annotation { "Feature Type Name" : "Feature", "Feature Type Description" : "" }
export const myFeature = defineFeature(function(context is Context, id is Id, definition is map)
    precondition{}
    {
        {
            var Q0;
            Q0=qCreatedBy(makeId("Top.planeOp"),FACE);
            var sketch = newSketch(context, id + "F0", { "sketchPlane" : qUnion([Q0])});
            skLineSegment(sketch, "E0.bottom", {"start": v(55, -37.5) * mm, "end": v(-55, -37.5) * mm});
            skLineSegment(sketch, "E0.top", {"start": v(55, 37.5) * mm, "end": v(-55, 37.5) * mm});
            skLineSegment(sketch, "E0.left", {"start": v(55, -37.5) * mm, "end": v(55, 37.5) * mm});
            skLineSegment(sketch, "E0.right", {"start": v(-55, -37.5) * mm, "end": v(-55, 37.5) * mm});
            skPoint(sketch, "E0.middle", {"position": v(0, 0) * mm});
            skSolve(sketch);
        }
        {
            var Q0;
            Q0=makeQuery(id+"F0.imprint","IMPRINT",FACE,{"disambiguationData":[TD([[makeQuery(id+"F0.imprint","IMPRINT",EDGE,{"derivedFrom":sQuery(id+"F0.wireOp",EDGE,"E0.bottom")}),-1.0]])]});
            extrude(context, id + "F1", {"entities" : qUnion([Q0]), "depth" : 3 * mm, "offsetDistance" : 25 * mm});
        }
        {
            var Q0;
            Q0=makeQuery(id+"F1.opExtrude","CAP_FACE",FACE,{"disambiguationData":[OSD([sQuery(id+"F0.wireOp",EDGE,"E0.bottom"),sQuery(id+"F0.wireOp",EDGE,"E0.top"),sQuery(id+"F0.wireOp",EDGE,"E0.left"),sQuery(id+"F0.wireOp",EDGE,"E0.right")])],"isStart":false});
            var sketch = newSketch(context, id + "F2", { "sketchPlane" : qUnion([Q0])});
            skLineSegment(sketch, "E1.bottom", {"start": v(-55, 37.5) * mm, "end": v(-50.5, 37.5) * mm});
            skLineSegment(sketch, "E1.left", {"start": v(-55, 37.5) * mm, "end": v(-55, 32.5) * mm});
            skLineSegment(sketch, "E2.bottom", {"start": v(-55, -37.5) * mm, "end": v(-50, -37.5) * mm});
            skLineSegment(sketch, "E2.left", {"start": v(-55, -37.5) * mm, "end": v(-55, -32.5) * mm});
            skLineSegment(sketch, "E3", {"start": v(0, 31.66) * mm, "end": v(0, -14.53) * mm, "construction": true});
            skLineSegment(sketch, "E4.MirrorCS", {"start": v(-50, -37.5) * mm, "end": v(-50, -32.5) * mm});
            skLineSegment(sketch, "E5.bottom", {"start": v(55, 37.5) * mm, "end": v(50, 37.5) * mm});
            skLineSegment(sketch, "E5.left", {"start": v(55, 37.5) * mm, "end": v(55, 32.5) * mm});
            skLineSegment(sketch, "E6.bottom", {"start": v(55, -37.5) * mm, "end": v(50, -37.5) * mm});
            skLineSegment(sketch, "E6.left", {"start": v(55, -37.5) * mm, "end": v(55, -32.5) * mm});
            skCircle(sketch, "E7", {"center": v(-50.5, 33) * mm, "radius": 1.5 * mm});
            skCircle(sketch, "E8", {"center": v(-50.5, -33) * mm, "radius": 1.5 * mm});
            skCircle(sketch, "E9", {"center": v(50.5, -33) * mm, "radius": 1.5 * mm});
            skCircle(sketch, "E10", {"center": v(50.5, 33) * mm, "radius": 1.5 * mm});
            skLineSegment(sketch, "E11", {"start": v(-50.5, 33) * mm, "end": v(-50.5, 37.5) * mm});
            skLineSegment(sketch, "E12", {"start": v(-50.5, 33) * mm, "end": v(-55, 33) * mm});
            skSolve(sketch);
        }
        {
            var Q0;
            Q0=makeQuery(id+"F2.imprint","IMPRINT",FACE,{"disambiguationData":[TD([[makeQuery(id+"F2.imprint","IMPRINT",EDGE,{"derivedFrom":sQuery(id+"F2.wireOp",EDGE,"E10")}),1.0]])]});
            var Q1;
            Q1=makeQuery(id+"F2.imprint","IMPRINT",FACE,{"disambiguationData":[TD([[makeQuery(id+"F2.imprint","IMPRINT",EDGE,{"derivedFrom":sQuery(id+"F2.wireOp",EDGE,"E9")}),1.0]])]});
            var Q2;
            Q2=makeQuery(id+"F2.imprint","IMPRINT",FACE,{"disambiguationData":[TD([[makeQuery(id+"F2.imprint","IMPRINT",EDGE,{"derivedFrom":sQuery(id+"F2.wireOp",EDGE,"E8")}),1.0]])]});
            var Q3;
            Q3=makeQuery(id+"F2.imprint","IMPRINT",FACE,{"disambiguationData":[TD([[makeQuery(id+"F2.imprint","IMPRINT",EDGE,{"derivedFrom":sQuery(id+"F2.wireOp",EDGE,"E7")}),1.0]])]});
            extrude(context, id + "F3", {"entities" : qUnion([Q0, Q1, Q2, Q3]), "operationType" : NewBodyOperationType.REMOVE, "oppositeDirection" : true, "depth" : 25 * mm, "offsetDistance" : 25 * mm});
        }
        {
            var Q0;
            Q0=makeQuery(id+"F1.opExtrude","CAP_FACE",FACE,{"disambiguationData":[OSD([sQuery(id+"F0.wireOp",EDGE,"E0.bottom"),sQuery(id+"F0.wireOp",EDGE,"E0.top"),sQuery(id+"F0.wireOp",EDGE,"E0.left"),sQuery(id+"F0.wireOp",EDGE,"E0.right")])],"isStart":false});
            var sketch = newSketch(context, id + "F4", { "sketchPlane" : qUnion([Q0])});
            skLineSegment(sketch, "E13", {"start": v(-55, -37.5) * mm, "end": v(-55, -13.42) * mm, "construction": true});
            skLineSegment(sketch, "E14", {"start": v(-55, 0) * mm, "end": v(-41.25, 0) * mm});
            skCircle(sketch, "E15", {"center": v(-41.25, 0) * mm, "radius": 6.8 * mm});
            skCircle(sketch, "E16.1.0.0", {"center": v(-13.75, 0) * mm, "radius": 6.8 * mm});
            skCircle(sketch, "E16.2.0.0", {"center": v(13.75, 0) * mm, "radius": 6.8 * mm});
            skCircle(sketch, "E16.3.0.0", {"center": v(41.25, 0) * mm, "radius": 6.8 * mm});
            skCircle(sketch, "E17", {"center": v(-27.5, -23.82) * mm, "radius": 6.8 * mm});
            skCircle(sketch, "E18.1.0.0", {"center": v(27.5, -23.82) * mm, "radius": 6.8 * mm});
            skLineSegment(sketch, "E19", {"start": v(-13.75, 0) * mm, "end": v(-41.25, 0) * mm});
            skLineSegment(sketch, "E20", {"start": v(13.75, 0) * mm, "end": v(41.25, 0) * mm});
            skLineSegment(sketch, "E21", {"start": v(-34.45, 0) * mm, "end": v(-35.15, 0) * mm});
            skLineSegment(sketch, "E22", {"start": v(-35.15, 0) * mm, "end": v(-35.15, 3) * mm});
            skLineSegment(sketch, "E23", {"start": v(-35.15, 3) * mm, "end": v(-35.15, -3) * mm});
            skLineSegment(sketch, "E24", {"start": v(-6.95, 0) * mm, "end": v(-7.65, 0) * mm});
            skLineSegment(sketch, "E25", {"start": v(20.55, 0) * mm, "end": v(19.85, 0) * mm});
            skLineSegment(sketch, "E26", {"start": v(48.05, 0) * mm, "end": v(47.35, 0) * mm});
            skLineSegment(sketch, "E27", {"start": v(27.5, -23.82) * mm, "end": v(34.3, -23.82) * mm, "construction": true});
            skLineSegment(sketch, "E28", {"start": v(34.3, -23.82) * mm, "end": v(32.9, -23.82) * mm});
            skLineSegment(sketch, "E29", {"start": v(-27.5, -23.82) * mm, "end": v(-20.7, -23.82) * mm, "construction": true});
            skLineSegment(sketch, "E30", {"start": v(-20.7, -23.82) * mm, "end": v(-22.7, -23.82) * mm});
            skLineSegment(sketch, "E31", {"start": v(-20.7, -23.82) * mm, "end": v(-21.4, -23.82) * mm});
            skLineSegment(sketch, "E32", {"start": v(34.3, -23.82) * mm, "end": v(33.6, -23.82) * mm});
            skLineSegment(sketch, "E33", {"start": v(-7.65, 0) * mm, "end": v(-7.65, 3) * mm});
            skLineSegment(sketch, "E34", {"start": v(-7.65, 3) * mm, "end": v(-7.65, -3) * mm});
            skLineSegment(sketch, "E35", {"start": v(19.85, 0) * mm, "end": v(19.85, 3) * mm});
            skLineSegment(sketch, "E36", {"start": v(19.85, 3) * mm, "end": v(19.85, -3) * mm});
            skLineSegment(sketch, "E37", {"start": v(47.35, 0) * mm, "end": v(47.35, 3) * mm});
            skLineSegment(sketch, "E38", {"start": v(47.35, 3) * mm, "end": v(47.35, -3) * mm});
            skLineSegment(sketch, "E39", {"start": v(33.6, -23.82) * mm, "end": v(33.6, -20.81) * mm});
            skLineSegment(sketch, "E40", {"start": v(33.6, -20.81) * mm, "end": v(33.6, -26.82) * mm});
            skLineSegment(sketch, "E41", {"start": v(-21.4, -23.82) * mm, "end": v(-21.4, -20.81) * mm});
            skLineSegment(sketch, "E42", {"start": v(-21.4, -20.81) * mm, "end": v(-21.4, -26.82) * mm});
            skLineSegment(sketch, "E43", {"start": v(-41.25, 0) * mm, "end": v(-13.75, 0) * mm});
            skSolve(sketch);
        }
        {
            var Q0;
            {var subQ0=sQuery(id+"F4.wireOp",EDGE,"E19");var subQ1=sQuery(id+"F4.wireOp",EDGE,"E14");var subQ2=makeQuery(id+"F4.imprint","INTERSECT",VERTEX,{"derivedFrom":[subQ1,subQ0]});Q0=makeQuery(id+"F4.imprint","IMPRINT",FACE,{"disambiguationData":[TD([[makeQuery(id+"F4.imprint","IMPRINT",EDGE,{"disambiguationData":[TD([[subQ2,1.0]])],"derivedFrom":subQ1}),1.0]])]});}
            var Q1;
            {var subQ0=sQuery(id+"F4.wireOp",EDGE,"E19");var subQ1=sQuery(id+"F4.wireOp",EDGE,"E14");var subQ2=makeQuery(id+"F4.imprint","INTERSECT",VERTEX,{"derivedFrom":[subQ1,subQ0]});Q1=makeQuery(id+"F4.imprint","IMPRINT",FACE,{"disambiguationData":[TD([[makeQuery(id+"F4.imprint","IMPRINT",EDGE,{"disambiguationData":[TD([[subQ2,1.0]])],"derivedFrom":subQ1}),-1.0]])]});}
            var Q2;
            {var subQ1=sQuery(id+"F4.wireOp",EDGE,"E16.1.0.0");var subQ3=makeQuery(id+"F4.imprint","IMPRINT",VERTEX,{"derivedFrom":subQ1});Q2=makeQuery(id+"F4.imprint","IMPRINT",FACE,{"disambiguationData":[TD([[makeQuery(id+"F4.imprint","IMPRINT",EDGE,{"disambiguationData":[TD([[subQ3,1.0]])],"derivedFrom":subQ1}),1.0]])]});}
            var Q3;
            {var subQ0=sQuery(id+"F4.wireOp",EDGE,"E36");var subQ1=sQuery(id+"F4.wireOp",EDGE,"E16.2.0.0");var subQ2=makeQuery(id+"F4.imprint","INTERSECT",VERTEX,{"disambiguationData":[OD(0.0)],"derivedFrom":[subQ1,subQ0]});Q3=makeQuery(id+"F4.imprint","IMPRINT",FACE,{"disambiguationData":[TD([[makeQuery(id+"F4.imprint","IMPRINT",EDGE,{"disambiguationData":[TD([[subQ2,-1.0]])],"derivedFrom":subQ1}),1.0]])]});}
            var Q4;
            {var subQ1=sQuery(id+"F4.wireOp",EDGE,"E16.3.0.0");var subQ3=makeQuery(id+"F4.imprint","IMPRINT",VERTEX,{"derivedFrom":subQ1});Q4=makeQuery(id+"F4.imprint","IMPRINT",FACE,{"disambiguationData":[TD([[makeQuery(id+"F4.imprint","IMPRINT",EDGE,{"disambiguationData":[TD([[subQ3,1.0]])],"derivedFrom":subQ1}),1.0]])]});}
            var Q5;
            {var subQ0=sQuery(id+"F4.wireOp",EDGE,"E40");var subQ1=sQuery(id+"F4.wireOp",EDGE,"E18.1.0.0");var subQ2=makeQuery(id+"F4.imprint","INTERSECT",VERTEX,{"disambiguationData":[OD(0.0)],"derivedFrom":[subQ1,subQ0]});Q5=makeQuery(id+"F4.imprint","IMPRINT",FACE,{"disambiguationData":[TD([[makeQuery(id+"F4.imprint","IMPRINT",EDGE,{"disambiguationData":[TD([[subQ2,-1.0]])],"derivedFrom":subQ1}),1.0]])]});}
            var Q6;
            {var subQ0=sQuery(id+"F4.wireOp",EDGE,"E42");var subQ1=sQuery(id+"F4.wireOp",EDGE,"E17");var subQ2=makeQuery(id+"F4.imprint","INTERSECT",VERTEX,{"disambiguationData":[OD(0.0)],"derivedFrom":[subQ1,subQ0]});Q6=makeQuery(id+"F4.imprint","IMPRINT",FACE,{"disambiguationData":[TD([[makeQuery(id+"F4.imprint","IMPRINT",EDGE,{"disambiguationData":[TD([[subQ2,-1.0]])],"derivedFrom":subQ1}),1.0]])]});}
            extrude(context, id + "F5", {"entities" : qUnion([Q0, Q1, Q2, Q3, Q4, Q5, Q6]), "operationType" : NewBodyOperationType.REMOVE, "oppositeDirection" : true, "depth" : 25 * mm, "offsetDistance" : 25 * mm});
        }
        {
            var Q0;
            Q0=makeQuery(id+"F1.opExtrude","CAP_FACE",FACE,{"disambiguationData":[OSD([sQuery(id+"F0.wireOp",EDGE,"E0.bottom"),sQuery(id+"F0.wireOp",EDGE,"E0.top"),sQuery(id+"F0.wireOp",EDGE,"E0.left"),sQuery(id+"F0.wireOp",EDGE,"E0.right")])],"isStart":false});
            var sketch = newSketch(context, id + "F6", { "sketchPlane" : qUnion([Q0])});
            skSolve(sketch);
        }
        {
            var Q0;
            Q0=makeQuery(id+"F6.imprint","IMPRINT",FACE,{"disambiguationData":[TD([[makeQuery(id+"F6.imprint","IMPRINT",EDGE,{"derivedFrom":makeQuery(id+"F1.opExtrude","CAP_EDGE",EDGE,{"disambiguationData":[OSD([sQuery(id+"F0.wireOp",EDGE,"E0.bottom")])],"isStart":false})}),-1.0]])]});
            var sketch = newSketch(context, id + "F7", { "sketchPlane" : qUnion([Q0])});
            skText(sketch, "E44", { "text": "Photonic Industries", "fontName": "AllertaStencil-Regular.ttf"});
            const initialGuessF7  = {"E44": [-0.04024, 0.02116, 1, 0, 0.006]};
            skSetInitialGuess(sketch, initialGuessF7);
            skSolve(sketch);
        }
        {
            var Q0;
            Q0 = qSketchRegion(id + "F7", true);
            extrude(context, id + "F8", {"entities" : qUnion([Q0]), "operationType" : NewBodyOperationType.ADD, "depth" : 0.6 * mm, "offsetDistance" : 25 * mm});
        }
        {
            var Q0;
            Q0=makeQuery(id+"F6.imprint","IMPRINT",FACE,{"disambiguationData":[TD([[makeQuery(id+"F6.imprint","IMPRINT",EDGE,{"derivedFrom":makeQuery(id+"F1.opExtrude","CAP_EDGE",EDGE,{"disambiguationData":[OSD([sQuery(id+"F0.wireOp",EDGE,"E0.bottom")])],"isStart":false})}),-1.0]])]});
            var sketch = newSketch(context, id + "F9", { "sketchPlane" : qUnion([Q0])});
            skText(sketch, "E45", { "text": "AR-6", "fontName": "OpenSans-Regular.ttf"});
            const initialGuessF9  = {"E45": [-0.01067, 0.01183, 1, 0, 0.00667]};
            skSetInitialGuess(sketch, initialGuessF9);
            skSolve(sketch);
        }
        {
            var Q0;
            Q0 = qSketchRegion(id + "F9", true);
            extrude(context, id + "F10", {"entities" : qUnion([Q0]), "operationType" : NewBodyOperationType.ADD, "depth" : 0.6 * mm, "offsetDistance" : 25 * mm});
        }
    });